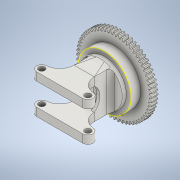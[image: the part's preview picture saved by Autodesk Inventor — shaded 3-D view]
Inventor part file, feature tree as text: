
AUTODESK INVENTOR PART (.ipt)
format: ipt  version: 2022 (Build 260153070, 153G)  size: 548,864 bytes
history: native  units: mm (DEFAULTED — no unit token found)
features: other x11, sketch x10, extrude x7, plane x5, reference x3, mirror x2, loft x1, fillet x1, projected_geometry x1
ambient origin geometry x8: Origin, YZ Plane, XZ Plane, XY Plane, X Axis, Y Axis, Z Axis, Center Point
bodies: Solid1 (feature_tree)
feature tree (41):
  extrude  "Extrusion1"  Depth=3.0mm TaperAngle=0.0deg
  plane  "Work Plane2"
  other  "Spur Gear"
  sketch  "Sketch4"  dims[d16=21.0mm d17=0.0mm]
  plane  "Work Plane11"
  extrude  "Extrusion3"  Depth=10.0mm TaperAngle=0.0deg
  plane  "Work Plane12"
  extrude  "Extrusion4"  TaperAngle=0.0deg  [1 undecoded]
  extrude  "Extrusion5"  Depth=21.0mm
  sketch  "Sketch7"  dims[d53=2.0mm d54=3.8mm d55=0.0mm]
  plane  "Work Plane13"
  other  "Work Point2"
  other  "Work Point3"
  extrude  "Extrusion6"  Depth=10.0mm TaperAngle=0.0deg
  plane  "Work Plane15"
  extrude  "Extrusion8"  Depth=2.0mm TaperAngle=0.0deg
  sketch  "Sketch13"  dims[d63=2.476182mm]
  loft  "Loft1"
  mirror  "Mirror2"
  extrude  "Extrusion9"  Depth=3.0mm
  mirror  "Mirror3"
  fillet  "Fillet1"  Radius=3.0mm
  sketch  "Sketch1"  dims[d0=37.2mm d1=3.0mm d2=0.0mm]
  sketch  "Sketch2"  dims[d3=36.0mm d4=10.0mm d5=0.0mm]
  other  "Srf1"
  reference  "Reference3"
  reference  "Reference4"
  sketch  "Sketch5"  dims[d41=0.0mm d43=21.0mm]
  sketch  "Sketch6"  dims[d46=21.0mm d51=10.0mm d52=0.0mm]
  projected_geometry  "Projected Loop1"
  other  "Work Point1"
  sketch  "Sketch10"  dims[d56=1.0mm d57=0.0mm d58=1.5mm]
  sketch  "Sketch12"  dims[d59=22.0mm d61=3.0mm d62=3.0mm]
  other  "Edges1"
  reference  "Reference8"
  sketch  "Sketch14"  dims[d64=2.5mm d65=2.5mm d66=1.0mm d67=1.0mm d69=4.0mm d70=0.0mm d71=22.74mm d73=10.0mm d74=10.0mm d75=6.372812mm d81=2.0mm d82=0.0mm d83=0.0mm d84=90.0deg d85=0.0mm d86=90.0deg d87=12.0mm d88=1.5mm d89=0.0mm d90=2.0mm]
  other  "Pitch Diameter"
  other  "<userpath> laptop\Desktop\SumoBot\sumobotLIDAR\sumobotLIDAR.iam"
  other  "sumobotLIDAR.iam"
  other  "608ZZ bearing:1"
  other  "Adapterlowerplate:1"
note: 1 required parameter value undecoded (feature->parameter linkage not recoverable at this tier; creation-order binding heuristic only, values carry confidence <= 0.55)
